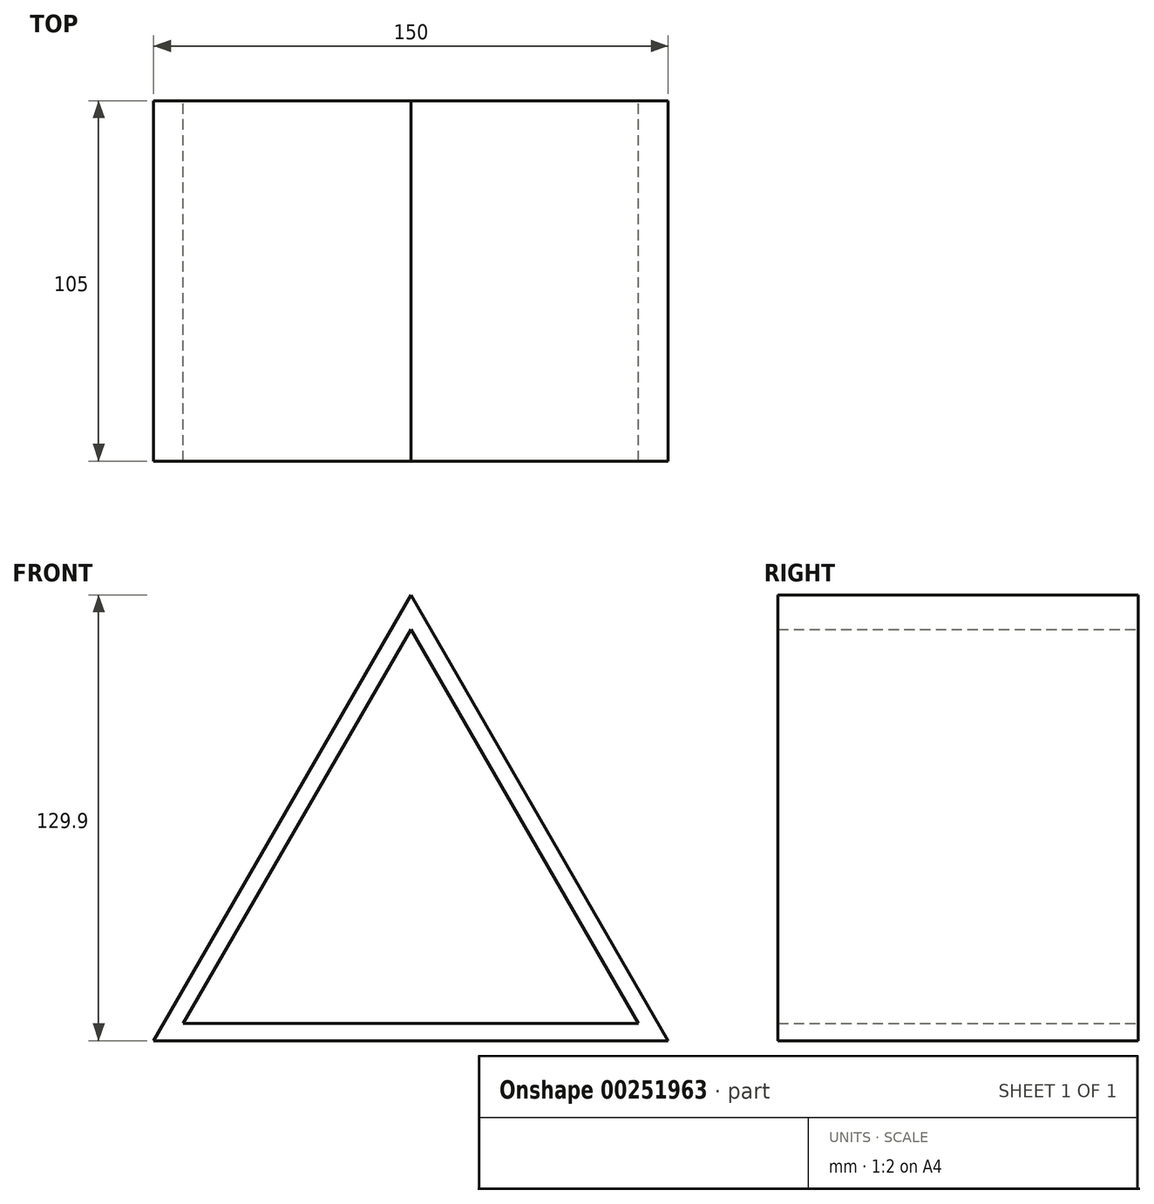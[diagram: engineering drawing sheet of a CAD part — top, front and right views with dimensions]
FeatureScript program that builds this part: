
annotation { "Feature Type Name" : "Feature", "Feature Type Description" : "" }
export const myFeature = defineFeature(function(context is Context, id is Id, definition is map)
    precondition{}
    {
        {
            var Q0;
            Q0=qCreatedBy(makeId("Front.planeOp"),FACE);
            var sketch = newSketch(context, id + "F0", { "sketchPlane" : qUnion([Q0])});
            skLineSegment(sketch, "E0", {"start": v(-74.76, -74.54) * mm, "end": v(75.24, -74.54) * mm});
            skLineSegment(sketch, "E1", {"start": v(75.24, -74.54) * mm, "end": v(0.24, 55.36) * mm});
            skLineSegment(sketch, "E2", {"start": v(0.24, 55.36) * mm, "end": v(-74.76, -74.54) * mm});
            skLineSegment(sketch, "E3.0", {"start": v(0.24, 45.36) * mm, "end": v(-66.1, -69.54) * mm});
            skLineSegment(sketch, "E3.1", {"start": v(66.58, -69.54) * mm, "end": v(0.24, 45.36) * mm});
            skLineSegment(sketch, "E3.2", {"start": v(-66.1, -69.54) * mm, "end": v(66.58, -69.54) * mm});
            skSolve(sketch);
        }
        {
            var Q0;
            Q0=makeQuery(id+"F0.imprint","IMPRINT",FACE,{"disambiguationData":[TD([[makeQuery(id+"F0.imprint","IMPRINT",EDGE,{"derivedFrom":sQuery(id+"F0.wireOp",EDGE,"E0")}),1.0]])]});
            extrude(context, id + "F1", {"entities" : qUnion([Q0]), "depth" : 105 * mm});
        }
    });
